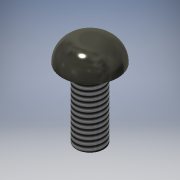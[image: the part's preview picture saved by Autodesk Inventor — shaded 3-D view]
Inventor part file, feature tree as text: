
AUTODESK INVENTOR PART (.ipt)
format: ipt  version: 2016 (Build 200138000, 138)  size: 143,360 bytes
history: native  units: mm
features: extrude x3, sketch x3, other x1, fillet x1, thread x1
ambient origin geometry x1: Origin
bodies: Body1 (feature_tree)
feature tree (9):
  other  "ソリッド1"
  extrude  "押し出し1"  Depth=4.0mm
  extrude  "押し出し2"  Depth=6.0mm TaperAngle=0.0deg
  fillet  "フィレット1"  Radius=8.0mm
  thread  "ねじ1"
  extrude  "押し出し3"  Depth=3.0mm TaperAngle=0.0deg
  sketch  "スケッチ1"
  sketch  "スケッチ2"
  sketch  "スケッチ3"
